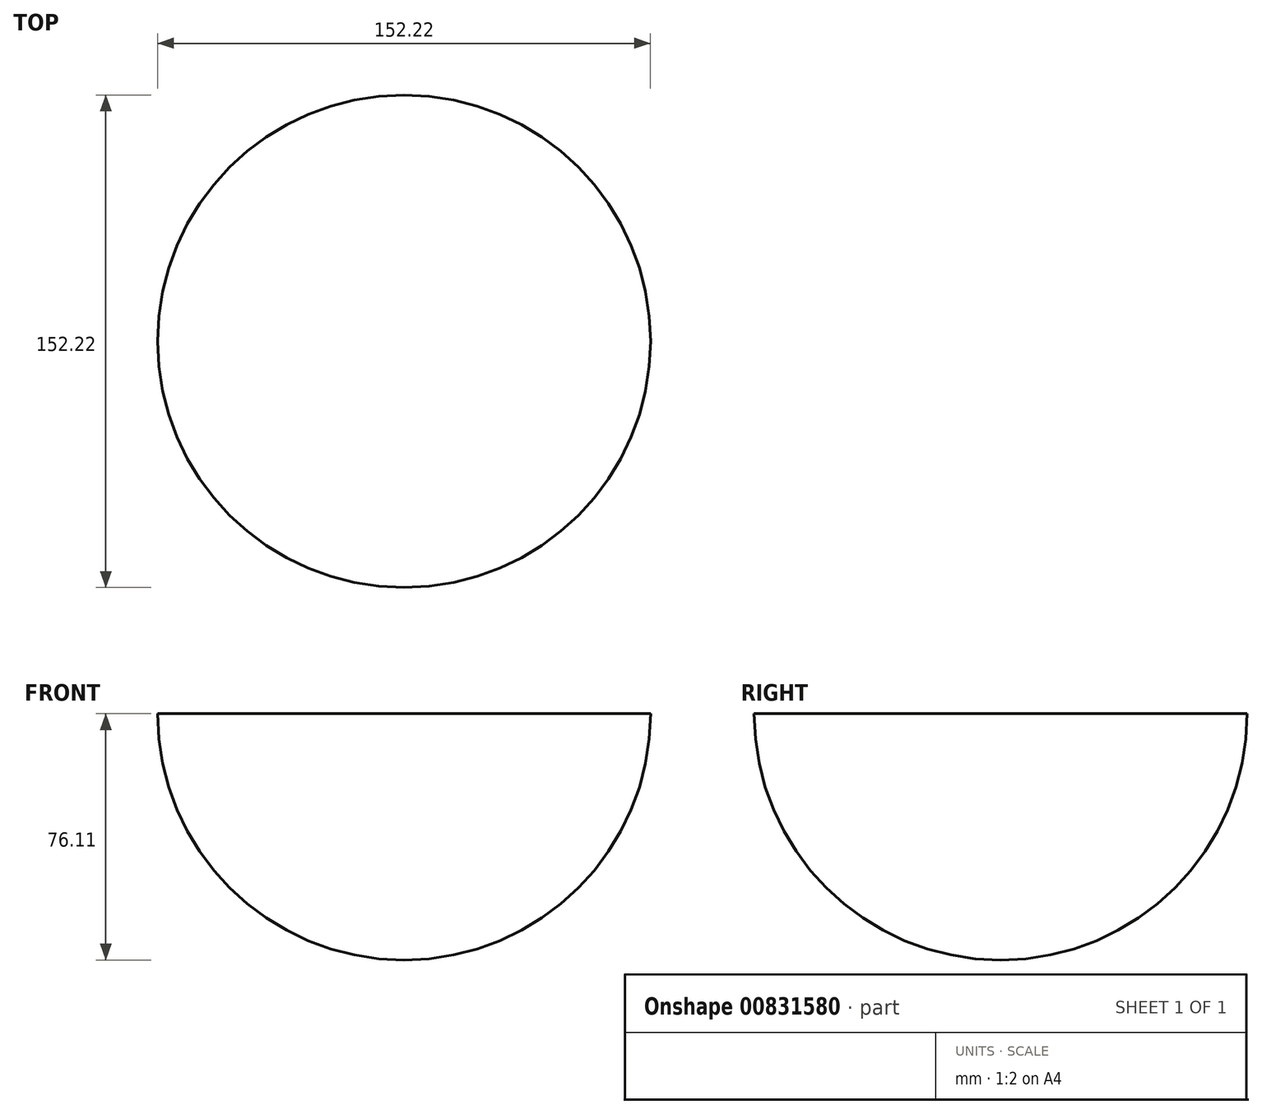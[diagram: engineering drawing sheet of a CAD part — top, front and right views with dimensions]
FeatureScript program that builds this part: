
annotation { "Feature Type Name" : "Feature", "Feature Type Description" : "" }
export const myFeature = defineFeature(function(context is Context, id is Id, definition is map)
    precondition{}
    {
        {
            var Q0;
            Q0=qCreatedBy(makeId("Top.planeOp"),FACE);
            var sketch = newSketch(context, id + "F0", { "sketchPlane" : qUnion([Q0])});
            skArc(sketch, "E0", {"start": v(0, 76.11) * mm, "mid": v(-76.11, 0) * mm, "end": v(0, -76.11) * mm});
            skLineSegment(sketch, "E1", {"start": v(0, 76.11) * mm, "end": v(0, -76.11) * mm});
            skSolve(sketch);
        }
        {
            var Q0;
            Q0 = qSketchRegion(id + "F0", true);
            var Q1;
            Q1=sQuery(id+"F0.wireOp",EDGE,"E1");
            revolve(context, id + "F1", {"surfaceOperationType" : NewSurfaceOperationType.NEW, "entities" : qUnion([Q0]), "axis" : qUnion([Q1]), "revolveType" : RevolveType.ONE_DIRECTION, "angle" : 180 * degree});
        }
    });
